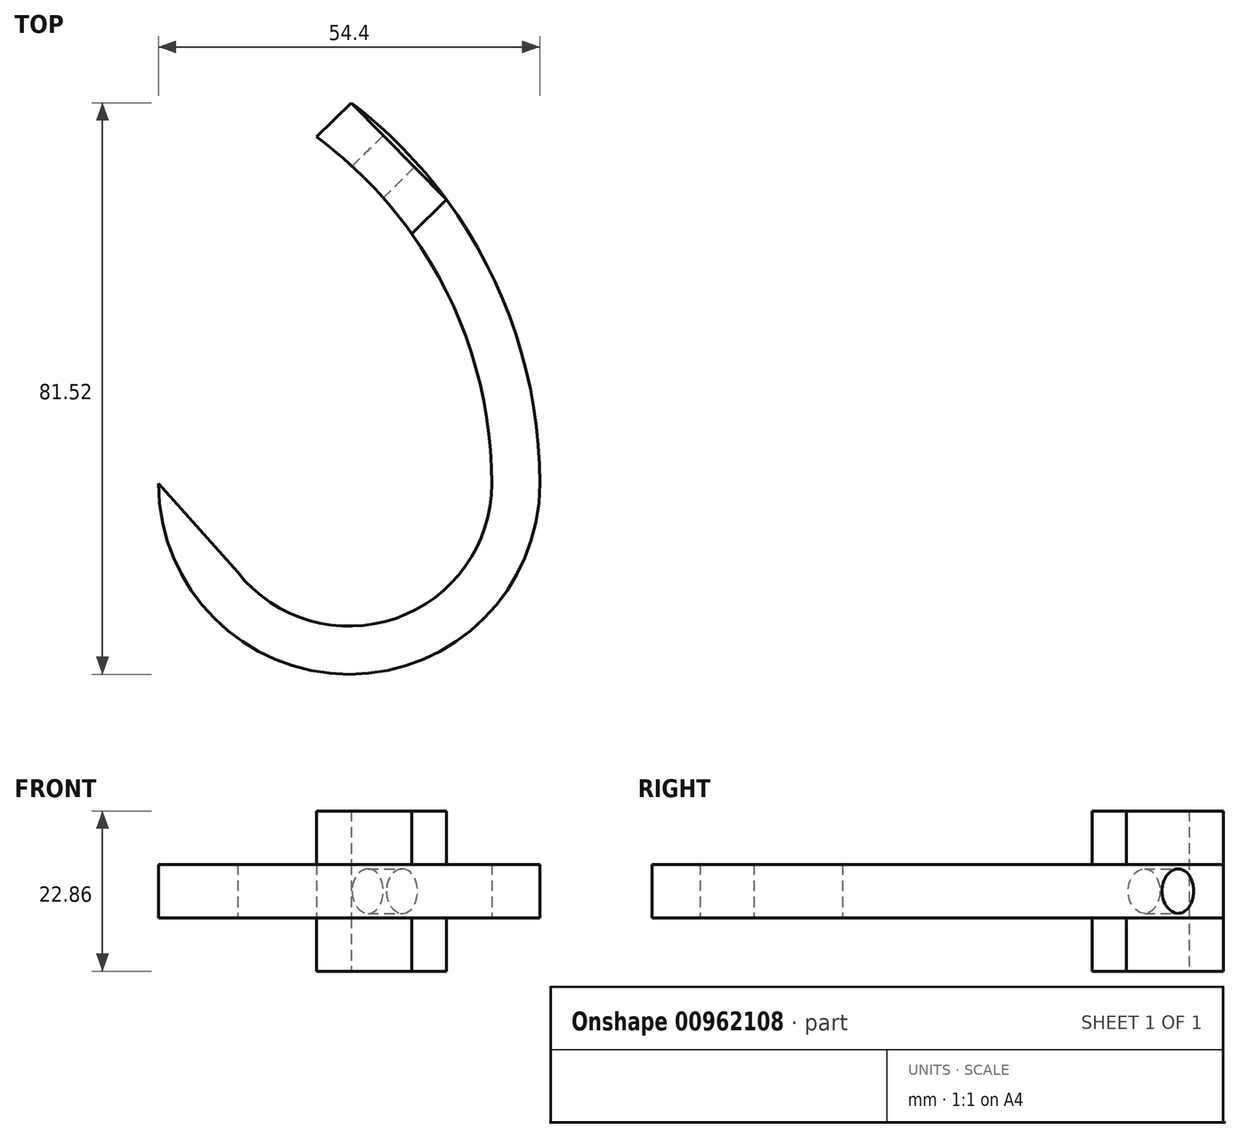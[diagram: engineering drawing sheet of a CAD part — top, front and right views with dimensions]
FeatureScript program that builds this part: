
annotation { "Feature Type Name" : "Feature", "Feature Type Description" : "" }
export const myFeature = defineFeature(function(context is Context, id is Id, definition is map)
    precondition{}
    {
        {
            var Q0;
            Q0=qCreatedBy(makeId("Top.planeOp"),FACE);
            var sketch = newSketch(context, id + "F0", { "sketchPlane" : qUnion([Q0])});
            skArc(sketch, "E0", {"start": v(5.55, -17.94) * mm, "mid": v(-1.05, 9.76) * mm, "end": v(-19.43, 31.51) * mm});
            skArc(sketch, "E1", {"start": v(-30.72, -30.58) * mm, "mid": v(-8.1, -37.14) * mm, "end": v(5.55, -17.94) * mm});
            skArc(sketch, "E2", {"start": v(-41.99, -17.94) * mm, "mid": v(-14.79, -45.14) * mm, "end": v(12.41, -17.94) * mm});
            skArc(sketch, "E3", {"start": v(12.41, -17.94) * mm, "mid": v(5.32, 12.37) * mm, "end": v(-14.48, 36.38) * mm});
            skLineSegment(sketch, "E4", {"start": v(-41.99, -17.94) * mm, "end": v(-30.72, -30.58) * mm});
            skLineSegment(sketch, "E5", {"start": v(-19.43, 31.51) * mm, "end": v(-14.48, 36.38) * mm});
            skSolve(sketch);
        }
        {
            var Q0;
            Q0=makeQuery(id+"F0.imprint","IMPRINT",FACE,{"disambiguationData":[TD([[makeQuery(id+"F0.imprint","IMPRINT",EDGE,{"derivedFrom":sQuery(id+"F0.wireOp",EDGE,"E0")}),-1.0]])]});
            extrude(context, id + "F1", {"entities" : qUnion([Q0]), "depth" : 7.62 * mm, "offsetDistance" : 25.4 * mm});
        }
        {
            var Q0;
            Q0=makeQuery(id+"F1.opExtrude","CAP_FACE",FACE,{"disambiguationData":[OSD([sQuery(id+"F0.wireOp",EDGE,"E0"),sQuery(id+"F0.wireOp",EDGE,"E1"),sQuery(id+"F0.wireOp",EDGE,"E2"),sQuery(id+"F0.wireOp",EDGE,"E3"),sQuery(id+"F0.wireOp",EDGE,"E4"),sQuery(id+"F0.wireOp",EDGE,"E5")])],"isStart":false});
            var sketch = newSketch(context, id + "F2", { "sketchPlane" : qUnion([Q0])});
            skLineSegment(sketch, "E6", {"start": v(-14.48, 36.38) * mm, "end": v(-19.43, 31.51) * mm});
            skLineSegment(sketch, "E7", {"start": v(-19.43, 31.51) * mm, "end": v(-5.84, 17.7) * mm});
            skLineSegment(sketch, "E8", {"start": v(-5.84, 17.7) * mm, "end": v(-0.9, 22.56) * mm});
            skLineSegment(sketch, "E9", {"start": v(-0.9, 22.56) * mm, "end": v(-14.48, 36.38) * mm});
            skSolve(sketch);
        }
        {
            var Q0;
            {var subQ0=sQuery(id+"F2.wireOp",EDGE,"E6");Q0=makeQuery(id+"F2.imprint","IMPRINT",FACE,{"disambiguationData":[TD([[makeQuery(id+"F2.imprint","IMPRINT",EDGE,{"derivedFrom":subQ0}),-1.0]])]});}
            extrude(context, id + "F3", {"entities" : qUnion([Q0]), "operationType" : NewBodyOperationType.ADD, "depth" : 7.62 * mm, "offsetDistance" : 25.4 * mm, "hasSecondDirection" : true, "secondDirectionOppositeDirection" : true, "secondDirectionDepth" : 15.24 * mm});
        }
        {
            var Q0;
            {var subQ0=sQuery(id+"F2.wireOp",EDGE,"E6");var subQ3=sQuery(id+"F0.wireOp",EDGE,"E0");var subQ4=sQuery(id+"F2.wireOp",EDGE,"E9");var subQ5=sQuery(id+"F2.wireOp",EDGE,"E8");Q0=makeQuery(id+"F3.boolean.opBoolean","SPLIT",FACE,{"disambiguationData":[TD([makeQuery(id+"F3.opExtrude","CAP_FACE",FACE,{"disambiguationData":[OSD([subQ3,subQ0,subQ5,subQ4])],"isStart":true})])],"derivedFrom":makeQuery(id+"F3.opExtrude","SWEPT_FACE",FACE,{"disambiguationData":[OSD([subQ4])]})});}
            var sketch = newSketch(context, id + "F4", { "sketchPlane" : qUnion([Q0])});
            skCircle(sketch, "E10", {"center": v(26.4, 3.8) * mm, "radius": 3.18 * mm});
            skPoint(sketch, "E10.centerSnap0", {"position": v(26.4, 0) * mm});
            skSolve(sketch);
        }
        {
            var Q0;
            Q0 = qSketchRegion(id + "F4", true);
            extrude(context, id + "F5", {"entities" : qUnion([Q0]), "operationType" : NewBodyOperationType.REMOVE, "oppositeDirection" : true, "depth" : 79.5 * mm, "offsetDistance" : 25.4 * mm, "hasSecondDirection" : true, "secondDirectionOppositeDirection" : false, "secondDirectionDepth" : 34.8 * mm});
        }
    });
